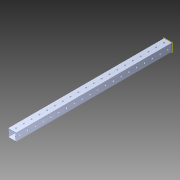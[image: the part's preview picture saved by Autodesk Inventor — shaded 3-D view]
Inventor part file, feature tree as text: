
AUTODESK INVENTOR PART (.ipt)
format: ipt  version: 2014 (Build 180170000, 170)  size: 1,276,416 bytes
history: native  units: in
note: dims shown in document units (in); Inventor stores cm internally (conversion verified against a paired STEP export)
features: extrude x2, sketch x2, pattern_circular x1, other x1, plane x1, imported_body x1
ambient origin geometry x8: Origin, YZ Plane, XZ Plane, XY Plane, X Axis, Y Axis, Z Axis, Center Point
bodies: Body1 (feature_tree)
feature tree (8):
  pattern_circular  "CirPattern2"
  other  "217-3426-STEP1"
  plane  "Work Plane1"
  extrude  "Extrusion1"  Depth=3937.0079in TaperAngle=0.0deg
  extrude  "Extrusion2"  [1 undecoded]
  imported_body  "Base1"
  sketch  "Sketch1"  dims[d0=-21.0in d1=3937.0079in d2=0.0in]
  sketch  "Sketch3"  dims[d3=1.0in d4=0.0in]
note: 1 required parameter value undecoded (feature->parameter linkage not recoverable at this tier; creation-order binding heuristic only, values carry confidence <= 0.55)
